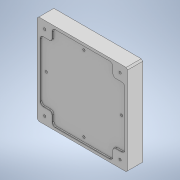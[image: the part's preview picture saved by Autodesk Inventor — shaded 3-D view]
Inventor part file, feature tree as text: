
AUTODESK INVENTOR PART (.ipt)
format: ipt  version: 2021 (Build 250183000, 183)  size: 199,680 bytes
history: native  units: mm
features: extrude x3, sketch x3, chamfer x2, fillet x1
ambient origin geometry x8: Origin, YZ Plane, XZ Plane, XY Plane, X Axis, Y Axis, Z Axis, Center Point
bodies: Solid1 (feature_tree)
feature tree (9):
  extrude  "Extrusion1"  Depth=300.0mm
  chamfer  "Chamfer1"  Distance=50.0mm
  extrude  "Extrusion2"  Depth=5.0mm
  extrude  "Extrusion3"  Depth=10.0mm
  fillet  "Fillet1"  Radius=7.5mm
  chamfer  "Chamfer2"  Distance=7.5mm
  sketch  "Sketch1"  dims[d0=300.0mm d1=300.0mm d2=50.0mm d3=0.0mm]
  sketch  "Sketch2"  dims[d4=5.0mm d5=2.0mm d6=45.0deg d7=25.0mm]
  sketch  "Sketch3"  dims[d8=125.0mm d9=25.0mm d10=7.5mm d11=7.5mm d12=7.5mm d13=0.0mm d14=0.0mm d15=10.0mm d16=10.0mm d17=50.0mm d18=50.0mm d19=5.0mm d20=0.0mm d21=10.0mm d22=1.0mm d23=2.0mm d24=45.0deg]
